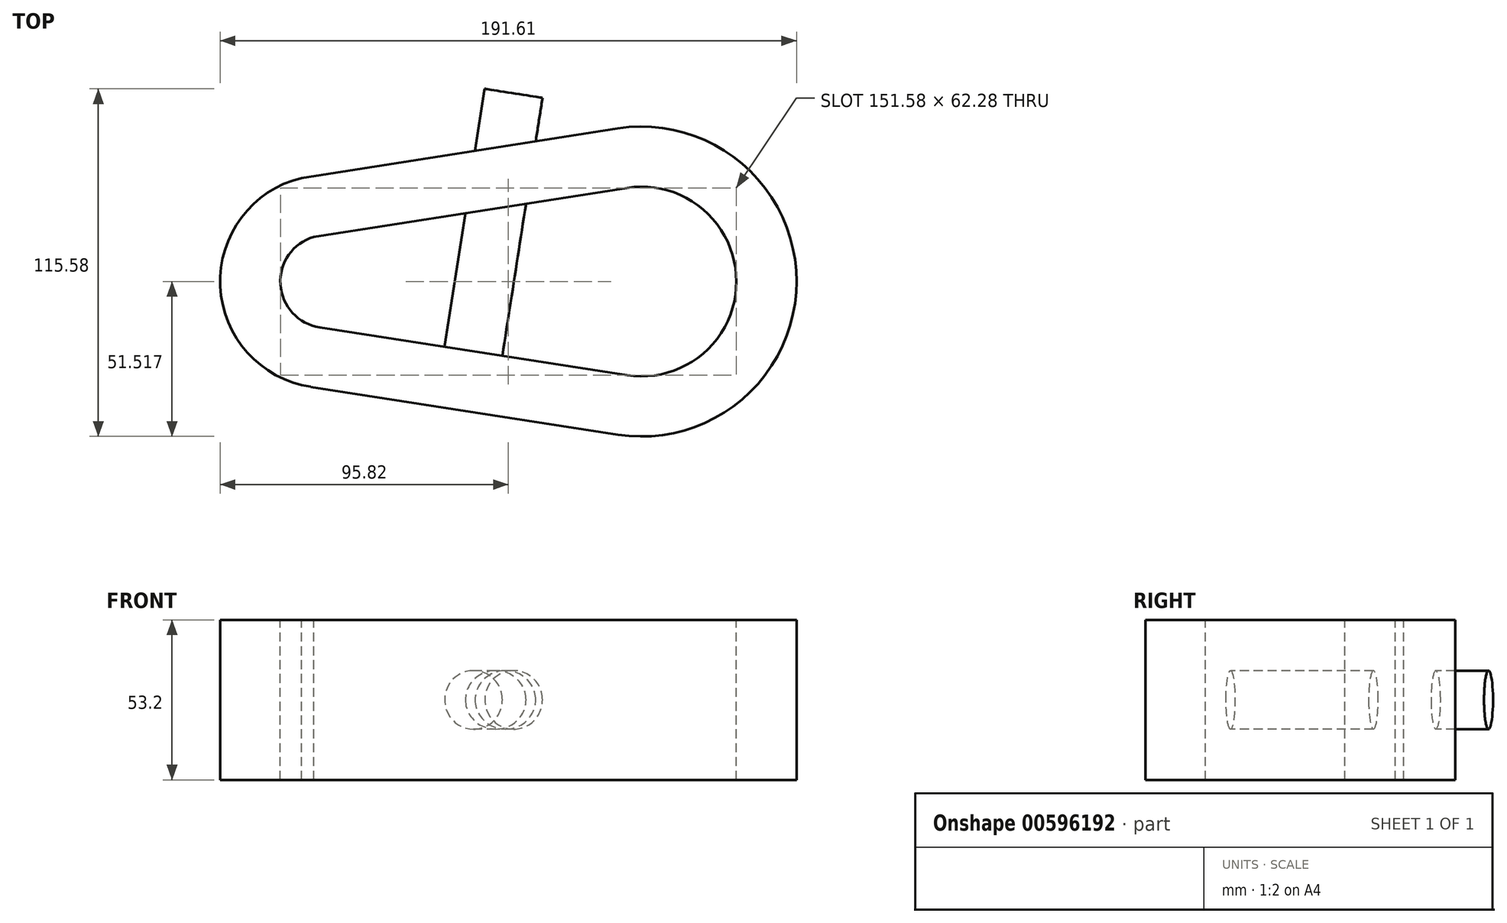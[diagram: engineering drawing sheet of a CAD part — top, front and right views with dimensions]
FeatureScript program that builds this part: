
annotation { "Feature Type Name" : "Feature", "Feature Type Description" : "" }
export const myFeature = defineFeature(function(context is Context, id is Id, definition is map)
    precondition{}
    {
        {
            var Q0;
            Q0=qCreatedBy(makeId("Top.planeOp"),FACE);
            var sketch = newSketch(context, id + "F0", { "sketchPlane" : qUnion([Q0])});
            skArc(sketch, "E0", {"start": v(-4.85, -31.14) * mm, "mid": v(31.52, 0.02) * mm, "end": v(-4.88, 31.14) * mm});
            skArc(sketch, "E1", {"start": v(-108.95, 14.82) * mm, "mid": v(-120.06, -1.02) * mm, "end": v(-106.96, -15.25) * mm});
            skLineSegment(sketch, "E2", {"start": v(-108.95, 14.82) * mm, "end": v(-4.88, 31.14) * mm});
            skLineSegment(sketch, "E3", {"start": v(-106.96, -15.25) * mm, "end": v(-4.85, -31.14) * mm});
            skLineSegment(sketch, "E4.0", {"start": v(-113.03, 34.42) * mm, "end": v(-7.95, 50.9) * mm});
            skArc(sketch, "E5.0", {"start": v(-7.92, -50.9) * mm, "mid": v(51.52, 0.01) * mm, "end": v(-7.95, 50.9) * mm});
            skLineSegment(sketch, "E6.0", {"start": v(-110.03, -35.02) * mm, "end": v(-7.92, -50.9) * mm});
            skArc(sketch, "E7.0", {"start": v(-113.03, 34.42) * mm, "mid": v(-140.06, -1.58) * mm, "end": v(-109.93, -35.03) * mm});
            skSolve(sketch);
        }
        {
            var Q0;
            Q0=makeQuery(id+"F0.imprint","IMPRINT",FACE,{"disambiguationData":[TD([[makeQuery(id+"F0.imprint","IMPRINT",EDGE,{"derivedFrom":sQuery(id+"F0.wireOp",EDGE,"E0")}),-1.0]])]});
            extrude(context, id + "F1", {"entities" : qUnion([Q0]), "oppositeDirection" : true, "depth" : 53.2 * mm, "offsetDistance" : 25 * mm});
        }
        {
            var Q0;
            Q0=makeQuery(id+"F1.opExtrude","SWEPT_FACE",FACE,{"disambiguationData":[OSD([sQuery(id+"F0.wireOp",EDGE,"E6.0")])]});
            var sketch = newSketch(context, id + "F2", { "sketchPlane" : qUnion([Q0])});
            skCircle(sketch, "E8", {"center": v(-51.65, -26.6) * mm, "radius": 9.72 * mm});
            skPoint(sketch, "E8.centerSnap0", {"position": v(-51.65, 0) * mm});
            skPoint(sketch, "E8.centerSnap1", {"position": v(-103.3, -26.6) * mm});
            skSolve(sketch);
        }
        {
            var Q0;
            Q0 = qSketchRegion(id + "F2", true);
            extrude(context, id + "F3", {"entities" : qUnion([Q0]), "operationType" : NewBodyOperationType.ADD, "oppositeDirection" : true, "depth" : 106.8 * mm, "offsetDistance" : 25 * mm});
        }
        {
            var Q0;
            Q0=makeQuery(id+"F3.opExtrude","CAP_FACE",FACE,{"disambiguationData":[OSD([sQuery(id+"F2.wireOp",EDGE,"E8")])],"isStart":false});
            extrude(context, id + "F4", {"entities" : qUnion([Q0]), "operationType" : NewBodyOperationType.ADD, "oppositeDirection" : true, "depth" : 33.4 * mm, "offsetDistance" : 25 * mm});
        }
    });
